# Revit family: LTV8EB
name_source: partatom
category: Lighting Fixtures
units: mm (PartAtom-declared; Revit-internal decimal feet)

## family parameters
Cut with Voids When Loaded = No
Host = Face
Light Source = Yes
OmniClass Number = 23.80.70.14.14
OmniClass Title = Exterior Floodlights
Part Type = Normal
Room Calculation Point = No
Round Connector Dimension = Use Diameter
Shared = No

## types (1)
- LTV81EB
    Apparent Load = 0 VA
    Certification = UL 1598 Standard for Luminaires.
■ UL 8750 Standard for Safety for Light
Emitting Diode (LED) Equipment for use
in Lighting Products.
    Color Filter = 16777215
    Default Elevation = 48.000"
    Description = RGBW Color Changing via Bluetooth® or DMX. The Lightvault 8 RGBW Eyeball provides additional tilt for illuminating signs and facades
    Dimming Lamp Color Temperature Shift = <None>
    Emit Shape Visible in Rendering = No
    Emit from Circle Diameter = 10.000"
    Features = Bluetooth connectivity for remote control aiming, dimming, color changing
Free mobile App for Adroid and iOS
X-Y tilt controls for aiming 12° in any direction
Variable dimming to 20% in 1% increments
IP68 sealed maintenance free LED light engine
One size: Large 13 inch
    Finish = Bronze
    Fixture = LTV8EB : LTV81EB
    Lamp = LED
    Lens = White Glass
    Manufacturer = Kim Lighting
    Model = Lightvault® LTV8EB Eyeball
    Nominal Watts = 31 W
    Photometric Web File = LTV81EB-NF-12RGBWUV.ies
    Tilt Angle = -90.00°
    URL = https://www.currentlighting.com
    Voltage = 120 V
    Warranty = 5 Years Limited Warranty

## geometry (parser evidence)
native form markers: Blend x4, Sweep x4
no freeform markers — native parametric forms only
